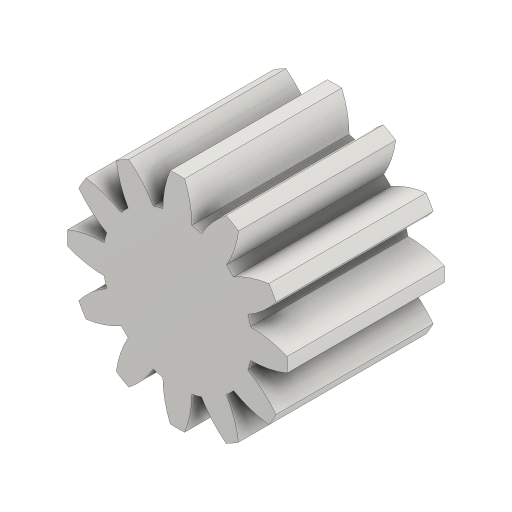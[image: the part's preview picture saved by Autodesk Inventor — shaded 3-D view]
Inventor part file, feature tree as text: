
AUTODESK INVENTOR PART (.ipt)
format: ipt  version: 2024 (Build 280153000, 153)  size: 243,200 bytes
history: native  units: mm (DEFAULTED — no unit token found)
features: plane x3, other x3, extrude x1, sketch x1
ambient origin geometry x8: Origin, YZ Plane, XZ Plane, XY Plane, X Axis, Y Axis, Z Axis, Center Point
bodies: Solid1 (feature_tree)
feature tree (8):
  extrude  "Extrusion1"  Depth=20.0mm TaperAngle=0.0deg
  plane  "Work Plane2"
  plane  "Work Plane8"
  plane  "Work Plane9"
  other  "Spur Gear"
  sketch  "Sketch1"  dims[d0=28.0mm d1=20.0mm d2=0.0mm d3=24.0mm d4=10.0mm d5=0.0mm d16=60.0mm d17=0.0mm d34=15.0deg d39=0.0mm d41=0.0mm d43=60.0mm d46=60.0mm d47=0.0mm d48=0.0mm]
  other  "Srf1"
  other  "Pitch Diameter"
